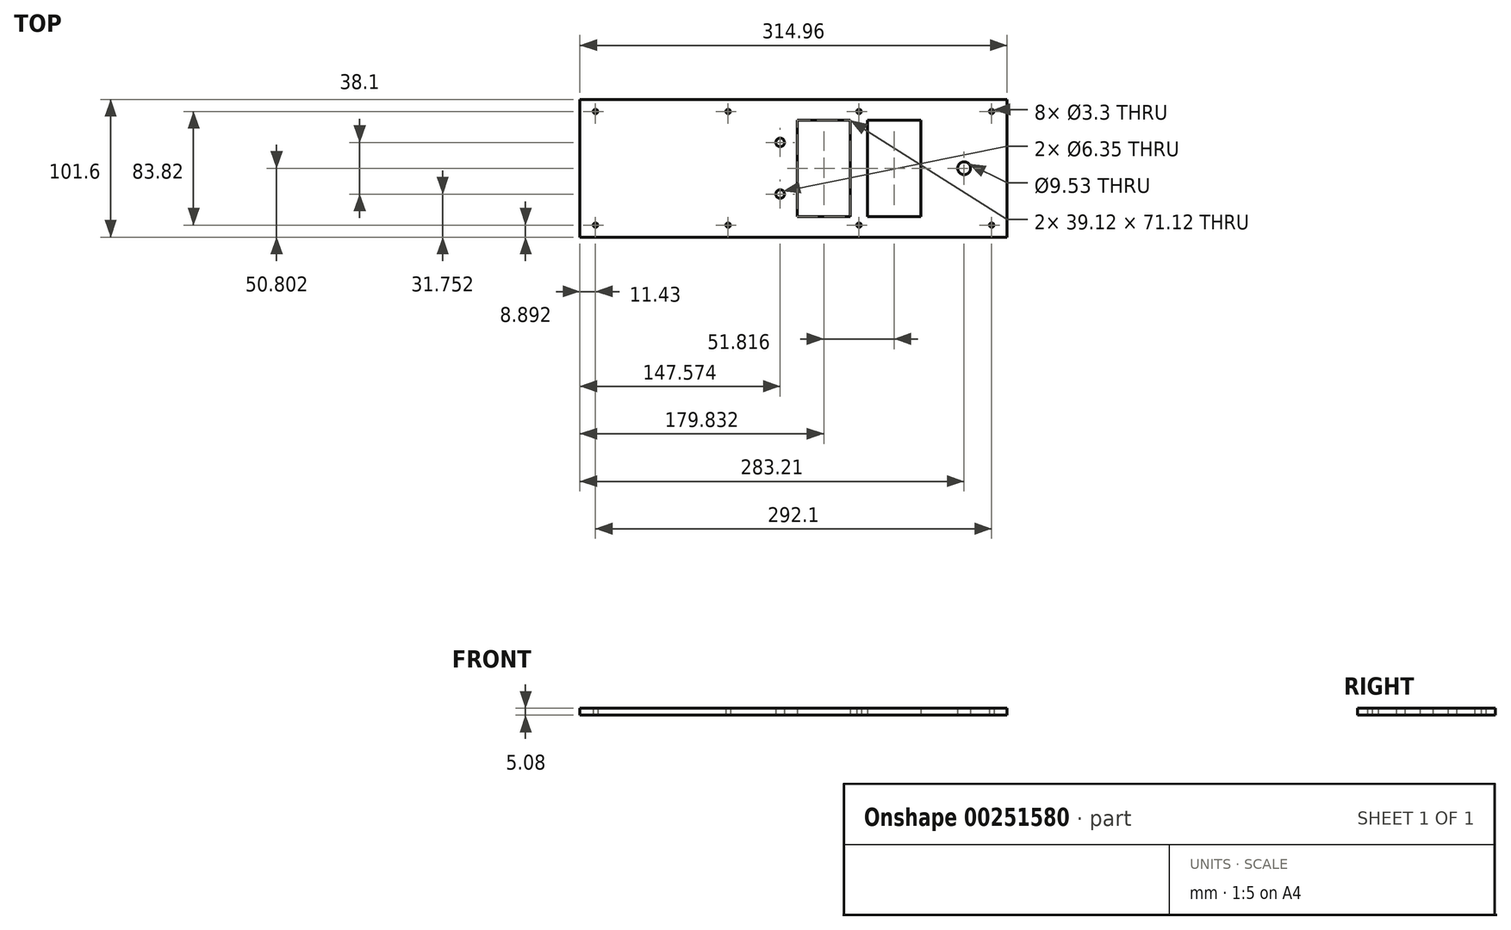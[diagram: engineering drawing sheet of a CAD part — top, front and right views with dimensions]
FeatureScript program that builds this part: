
annotation { "Feature Type Name" : "Feature", "Feature Type Description" : "" }
export const myFeature = defineFeature(function(context is Context, id is Id, definition is map)
    precondition{}
    {
        {
            var Q0;
            Q0=qCreatedBy(makeId("Top.planeOp"),FACE);
            var sketch = newSketch(context, id + "F0", { "sketchPlane" : qUnion([Q0])});
            skLineSegment(sketch, "E0.bottom", {"start": v(-132.08, 42.7) * mm, "end": v(182.88, 42.7) * mm});
            skLineSegment(sketch, "E0.top", {"start": v(-132.08, -58.9) * mm, "end": v(182.88, -58.9) * mm});
            skLineSegment(sketch, "E0.left", {"start": v(-132.08, 42.7) * mm, "end": v(-132.08, -58.9) * mm});
            skLineSegment(sketch, "E0.right", {"start": v(182.88, 42.7) * mm, "end": v(182.88, -58.9) * mm});
            skPoint(sketch, "E1", {"position": v(-120.65, 33.8) * mm});
            skPoint(sketch, "E2", {"position": v(-22.86, 33.8) * mm});
            skPoint(sketch, "E3", {"position": v(73.66, 33.8) * mm});
            skPoint(sketch, "E4", {"position": v(171.45, 33.8) * mm});
            skPoint(sketch, "E5", {"position": v(-120.65, -50.02) * mm});
            skPoint(sketch, "E6", {"position": v(-22.86, -50.02) * mm});
            skPoint(sketch, "E7", {"position": v(73.66, -50.02) * mm});
            skPoint(sketch, "E8", {"position": v(171.45, -50.02) * mm});
            skLineSegment(sketch, "E9.bottom", {"start": v(28.03, 27.45) * mm, "end": v(67.3, 27.45) * mm});
            skLineSegment(sketch, "E9.top", {"start": v(28.2, -43.67) * mm, "end": v(67.3, -43.67) * mm});
            skLineSegment(sketch, "E9.left", {"start": v(28.2, 27.45) * mm, "end": v(28.2, -43.67) * mm});
            skLineSegment(sketch, "E9.right", {"start": v(67.3, 27.45) * mm, "end": v(67.3, -43.67) * mm});
            skLineSegment(sketch, "E10.bottom", {"start": v(80, 27.45) * mm, "end": v(119.13, 27.45) * mm});
            skLineSegment(sketch, "E10.top", {"start": v(80, -43.67) * mm, "end": v(119.13, -43.67) * mm});
            skLineSegment(sketch, "E10.left", {"start": v(80, 27.45) * mm, "end": v(80, -43.67) * mm});
            skLineSegment(sketch, "E10.right", {"start": v(119.13, 27.45) * mm, "end": v(119.13, -43.67) * mm});
            skCircle(sketch, "E11", {"center": v(151.13, -8.1) * mm, "radius": 4.76 * mm});
            skPoint(sketch, "E11.centerSnap0", {"position": v(119.13, -8.1) * mm});
            skPoint(sketch, "E12", {"position": v(84.77, 22.53) * mm});
            skPoint(sketch, "E13", {"position": v(114.36, 22.53) * mm});
            skPoint(sketch, "E14", {"position": v(84.77, -39.07) * mm});
            skPoint(sketch, "E15", {"position": v(114.36, -38.9) * mm});
            skPoint(sketch, "E16", {"position": v(15.5, 10.94) * mm});
            skPoint(sketch, "E17", {"position": v(15.5, -27.16) * mm});
            skPoint(sketch, "E18.visualSharp", {"position": v(28.2, 27.45) * mm});
            skSolve(sketch);
        }
        {
            var Q0;
            Q0=makeQuery(id+"F0.imprint","IMPRINT",FACE,{"disambiguationData":[TD([[makeQuery(id+"F0.imprint","IMPRINT",EDGE,{"derivedFrom":sQuery(id+"F0.wireOp",EDGE,"E0.bottom")}),-1.0]])]});
            extrude(context, id + "F1", {"entities" : qUnion([Q0]), "depth" : 5.08 * mm});
        }
        {
            var Q0;
            Q0=sQuery(id+"F0.wireOp",VERTEX,"E1");
            var Q1;
            Q1=sQuery(id+"F0.wireOp",VERTEX,"E2");
            var Q2;
            Q2=sQuery(id+"F0.wireOp",VERTEX,"E3");
            var Q3;
            Q3=sQuery(id+"F0.wireOp",VERTEX,"E4");
            var Q4;
            Q4=sQuery(id+"F0.wireOp",VERTEX,"E8");
            var Q5;
            Q5=sQuery(id+"F0.wireOp",VERTEX,"E7");
            var Q6;
            Q6=sQuery(id+"F0.wireOp",VERTEX,"E6");
            var Q7;
            Q7=sQuery(id+"F0.wireOp",VERTEX,"E5");
            var Q8;
            Q8=makeQuery(id+"F1.opExtrude","SWEPT_BODY",BODY,{"disambiguationData":[OSD([sQuery(id+"F0.wireOp",EDGE,"E0.bottom"),sQuery(id+"F0.wireOp",EDGE,"E0.top"),sQuery(id+"F0.wireOp",EDGE,"E0.left"),sQuery(id+"F0.wireOp",EDGE,"E0.right")])]});
            hole(context, id + "F2", {"style" : HoleStyle.SIMPLE, "endStyle" : HoleEndStyle.THROUGH, "oppositeDirection" : true, "holeDiameter" : 3.3 * mm, "tappedDepth" : 12.7 * mm, "tapClearance" : 3, "startFromSketch" : true, "locations" : qUnion([Q0, Q1, Q2, Q3, Q4, Q5, Q6, Q7]), "scope" : qUnion([Q8])});
        }
        {
            var Q0;
            Q0=sQuery(id+"F0.wireOp",VERTEX,"E16");
            var Q1;
            Q1=sQuery(id+"F0.wireOp",VERTEX,"E17");
            var Q2;
            Q2=makeQuery(id+"F1.opExtrude","SWEPT_BODY",BODY,{"disambiguationData":[OSD([sQuery(id+"F0.wireOp",EDGE,"E0.bottom"),sQuery(id+"F0.wireOp",EDGE,"E0.top"),sQuery(id+"F0.wireOp",EDGE,"E0.left"),sQuery(id+"F0.wireOp",EDGE,"E0.right"),sQuery(id+"F0.wireOp",EDGE,"E9.bottom"),sQuery(id+"F0.wireOp",EDGE,"E9.top"),sQuery(id+"F0.wireOp",EDGE,"E9.left"),sQuery(id+"F0.wireOp",EDGE,"E9.right"),sQuery(id+"F0.wireOp",EDGE,"E10.bottom"),sQuery(id+"F0.wireOp",EDGE,"E10.top"),sQuery(id+"F0.wireOp",EDGE,"E10.left"),sQuery(id+"F0.wireOp",EDGE,"E10.right"),sQuery(id+"F0.wireOp",EDGE,"E11")])]});
            hole(context, id + "F3", {"style" : HoleStyle.SIMPLE, "endStyle" : HoleEndStyle.THROUGH, "oppositeDirection" : true, "holeDiameter" : 6.35 * mm, "tappedDepth" : 12.7 * mm, "tapClearance" : 3, "startFromSketch" : true, "locations" : qUnion([Q0, Q1]), "scope" : qUnion([Q2])});
        }
    });
